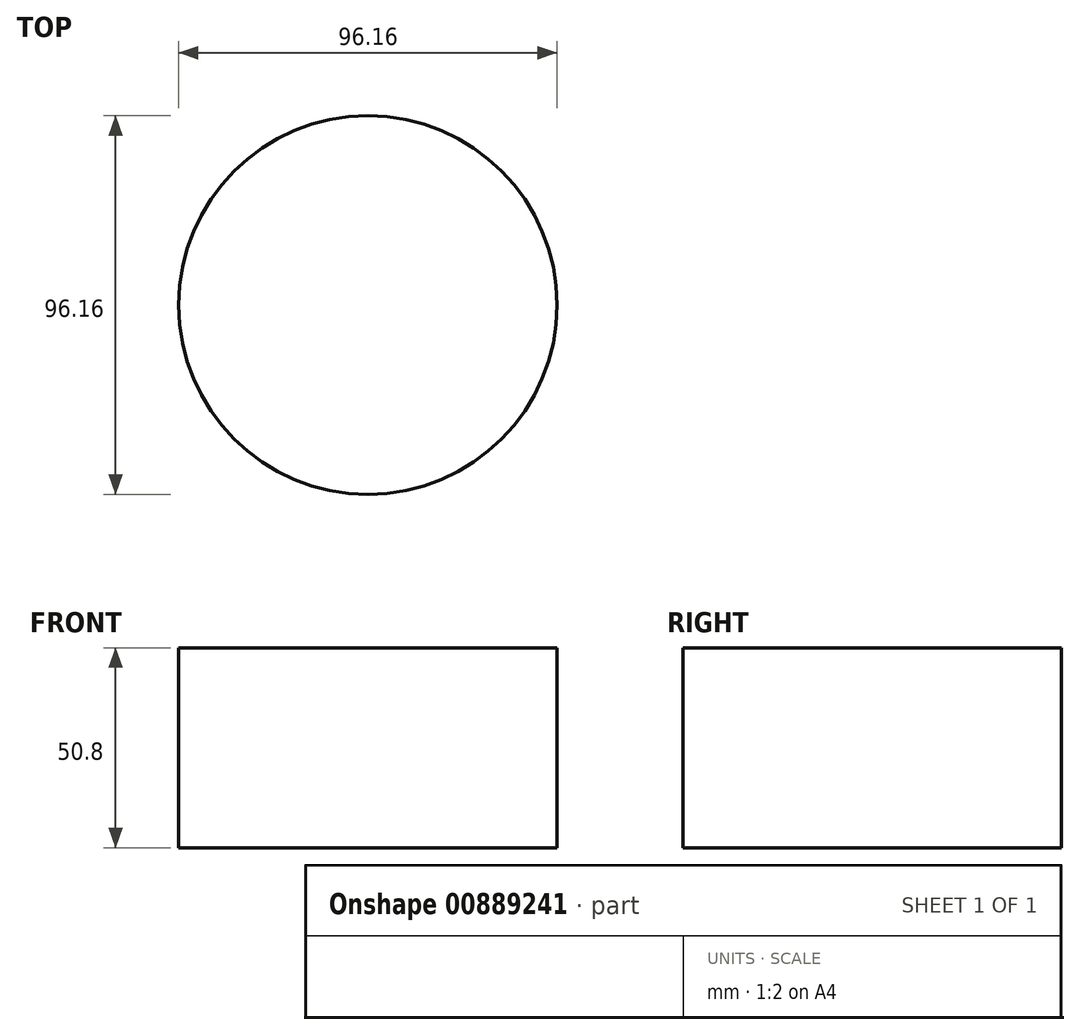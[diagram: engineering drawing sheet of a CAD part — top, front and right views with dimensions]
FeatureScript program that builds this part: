
annotation { "Feature Type Name" : "Feature", "Feature Type Description" : "" }
export const myFeature = defineFeature(function(context is Context, id is Id, definition is map)
    precondition{}
    {
        {
            var Q0;
            Q0=qCreatedBy(makeId("Top.planeOp"),FACE);
            var sketch = newSketch(context, id + "F0", { "sketchPlane" : qUnion([Q0])});
            skCircle(sketch, "E0", {"center": v(0, 0) * mm, "radius": 48.08 * mm});
            skSolve(sketch);
        }
        {
            var Q0;
            Q0=makeQuery(id+"F0.imprint","IMPRINT",FACE,{"disambiguationData":[TD([[makeQuery(id+"F0.imprint","IMPRINT",EDGE,{"derivedFrom":sQuery(id+"F0.wireOp",EDGE,"E0")}),1.0]])]});
            extrude(context, id + "F1", {"entities" : qUnion([Q0]), "depth" : 50.8 * mm, "offsetDistance" : 25.4 * mm});
        }
    });
